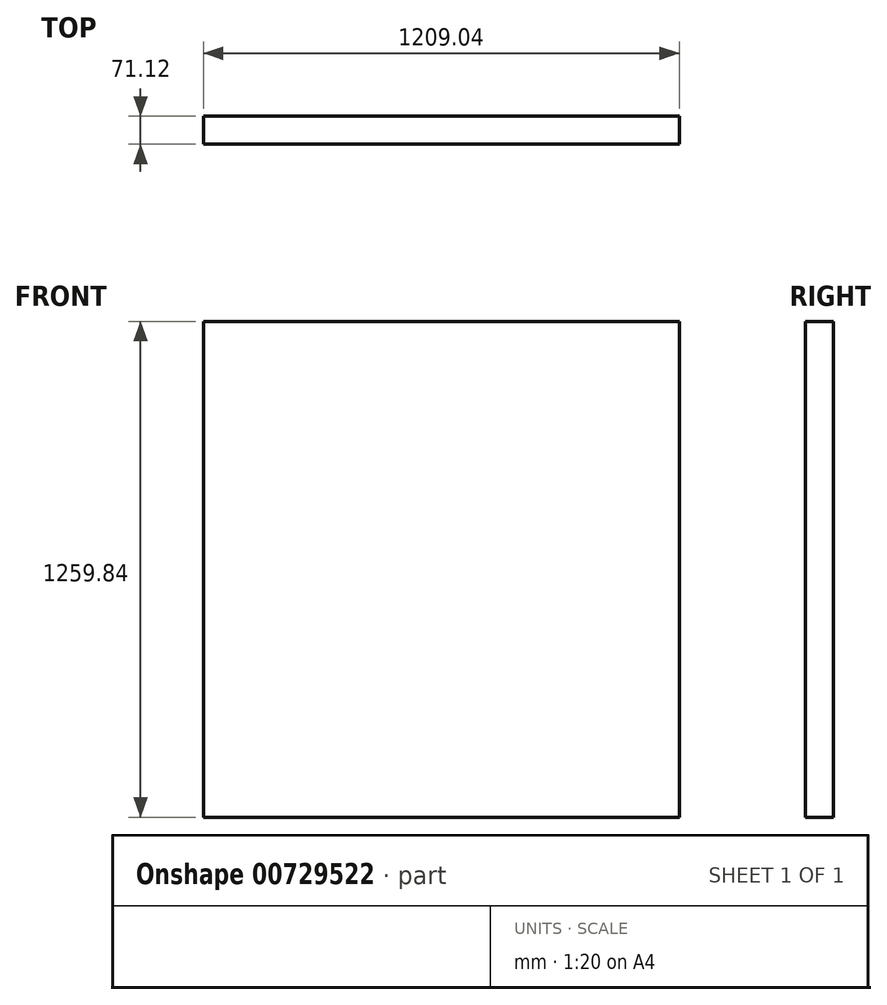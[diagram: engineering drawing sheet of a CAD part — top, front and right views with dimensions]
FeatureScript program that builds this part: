
annotation { "Feature Type Name" : "Feature", "Feature Type Description" : "" }
export const myFeature = defineFeature(function(context is Context, id is Id, definition is map)
    precondition{}
    {
        {
            var Q0;
            Q0=qCreatedBy(makeId("Front.planeOp"),FACE);
            var sketch = newSketch(context, id + "F0", { "sketchPlane" : qUnion([Q0])});
            skLineSegment(sketch, "E0.bottom", {"start": v(0, 0) * mm, "end": v(1209.04, 0) * mm});
            skLineSegment(sketch, "E0.top", {"start": v(0, 1259.84) * mm, "end": v(1209.04, 1259.84) * mm});
            skLineSegment(sketch, "E0.left", {"start": v(0, 0) * mm, "end": v(0, 1259.84) * mm});
            skLineSegment(sketch, "E0.right", {"start": v(1209.04, 0) * mm, "end": v(1209.04, 1259.84) * mm});
            skSolve(sketch);
        }
        {
            var Q0;
            Q0 = qSketchRegion(id + "F0", true);
            extrude(context, id + "F1", {"entities" : qUnion([Q0]), "depth" : 45.72 * mm, "offsetDistance" : 25.4 * mm, "hasSecondDirection" : true, "secondDirectionOppositeDirection" : true, "secondDirectionDepth" : 25.4 * mm});
        }
    });
